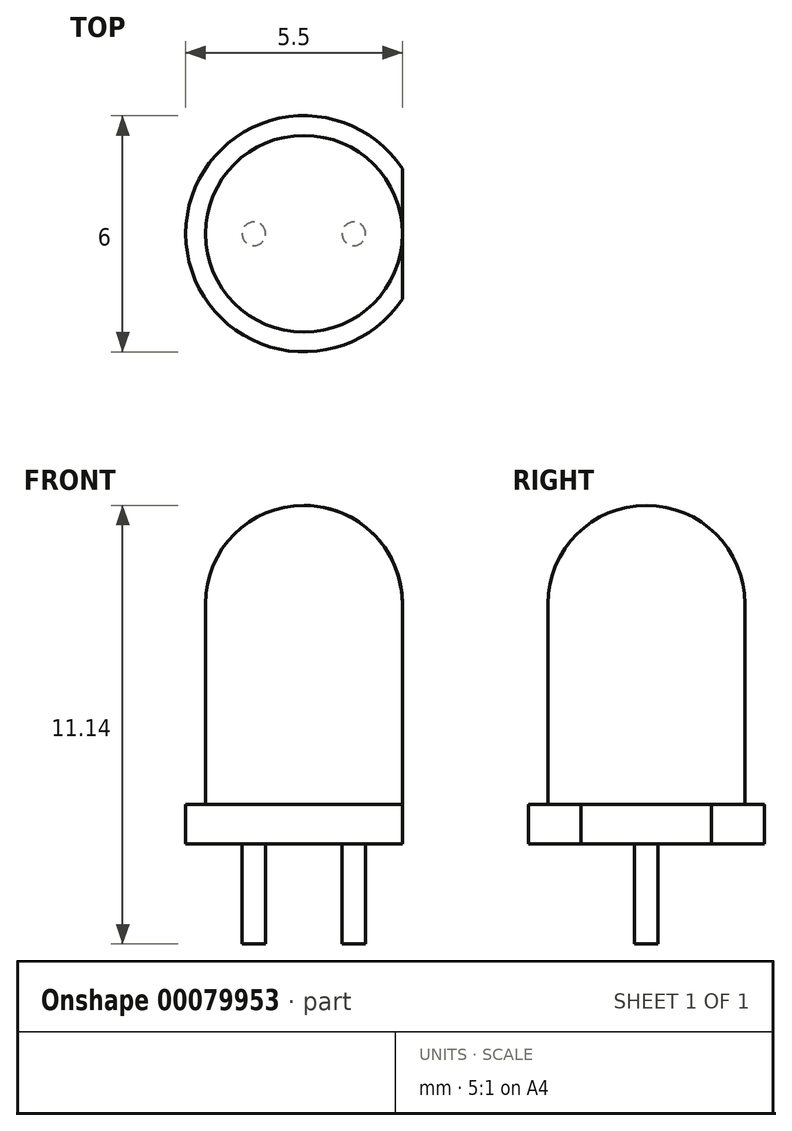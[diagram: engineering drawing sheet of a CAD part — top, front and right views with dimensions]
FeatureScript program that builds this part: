
annotation { "Feature Type Name" : "Feature", "Feature Type Description" : "" }
export const myFeature = defineFeature(function(context is Context, id is Id, definition is map)
    precondition{}
    {
        {
            var Q0;
            Q0=qCreatedBy(makeId("Top.planeOp"),FACE);
            var sketch = newSketch(context, id + "F0", { "sketchPlane" : qUnion([Q0])});
            skCircle(sketch, "E0", {"center": v(0, 0) * mm, "radius": 2.5 * mm});
            skCircle(sketch, "E1", {"center": v(0, 0) * mm, "radius": 3 * mm});
            skLineSegment(sketch, "E2", {"start": v(-1.27, 0) * mm, "end": v(1.27, 0) * mm});
            skCircle(sketch, "E3", {"center": v(-1.27, 0) * mm, "radius": 0.3 * mm});
            skCircle(sketch, "E4", {"center": v(1.27, 0) * mm, "radius": 0.3 * mm});
            skLineSegment(sketch, "E5", {"start": v(2.5, -1.66) * mm, "end": v(2.5, 1.66) * mm});
            skLineSegment(sketch, "E6", {"start": v(-2.69, -1.34) * mm, "end": v(0.18, -3) * mm});
            skLineSegment(sketch, "E7", {"start": v(-2.69, 1.34) * mm, "end": v(0.18, 3) * mm});
            skCircle(sketch, "E8", {"center": v(-0.64, -1.1) * mm, "radius": 0.3 * mm});
            skCircle(sketch, "E9", {"center": v(0.64, -1.1) * mm, "radius": 0.3 * mm});
            skCircle(sketch, "E10", {"center": v(0.64, 1.1) * mm, "radius": 0.3 * mm});
            skCircle(sketch, "E11", {"center": v(-0.64, 1.1) * mm, "radius": 0.3 * mm});
            skLineSegment(sketch, "E12", {"start": v(-0.64, -1.1) * mm, "end": v(-1.27, 0) * mm});
            skLineSegment(sketch, "E13", {"start": v(-0.64, -1.1) * mm, "end": v(0.64, -1.1) * mm});
            skLineSegment(sketch, "E14", {"start": v(0.63, -1.1) * mm, "end": v(1.27, 0) * mm});
            skLineSegment(sketch, "E15", {"start": v(1.27, 0) * mm, "end": v(0.63, 1.1) * mm});
            skLineSegment(sketch, "E16", {"start": v(-0.64, 1.1) * mm, "end": v(0.64, 1.1) * mm});
            skLineSegment(sketch, "E17", {"start": v(-0.64, 1.1) * mm, "end": v(-1.27, 0) * mm});
            skLineSegment(sketch, "E18", {"start": v(-0.64, -1.1) * mm, "end": v(0.64, 1.1) * mm});
            skLineSegment(sketch, "E19", {"start": v(-0.63, 1.1) * mm, "end": v(0.63, -1.1) * mm});
            skSolve(sketch);
        }
        {
            var Q0;
            Q0=makeQuery(id+"F0.imprint","IMPRINT",FACE,{"disambiguationData":[TD([[makeQuery(id+"F0.imprint","IMPRINT",EDGE,{"derivedFrom":sQuery(id+"F0.wireOp",EDGE,"E0")}),1.0]])]});
            var Q1;
            Q1=makeQuery(id+"F0.imprint","IMPRINT",FACE,{"disambiguationData":[TD([[makeQuery(id+"F0.imprint","IMPRINT",EDGE,{"derivedFrom":sQuery(id+"F0.wireOp",EDGE,"E3")}),1.0]])]});
            var Q2;
            Q2=makeQuery(id+"F0.imprint","IMPRINT",FACE,{"disambiguationData":[TD([[makeQuery(id+"F0.imprint","IMPRINT",EDGE,{"derivedFrom":sQuery(id+"F0.wireOp",EDGE,"E4")}),1.0]])]});
            var Q3;
            {var subQ1=sQuery(id+"F0.wireOp",EDGE,"E3");var subQ7=sQuery(id+"F0.wireOp",EDGE,"E2");var subQ8=makeQuery(id+"F0.imprint","INTERSECT",VERTEX,{"derivedFrom":[subQ7,subQ1]});Q3=makeQuery(id+"F0.imprint","IMPRINT",FACE,{"disambiguationData":[TD([[makeQuery(id+"F0.imprint","IMPRINT",EDGE,{"disambiguationData":[TD([[subQ8,1.0]])],"derivedFrom":subQ1}),-1.0]])]});}
            var Q4;
            {var subQ0=sQuery(id+"F0.wireOp",EDGE,"E18");var subQ1=sQuery(id+"F0.wireOp",EDGE,"E8");var subQ2=makeQuery(id+"F0.imprint","INTERSECT",VERTEX,{"derivedFrom":[subQ1,subQ0]});Q4=makeQuery(id+"F0.imprint","IMPRINT",FACE,{"disambiguationData":[TD([[makeQuery(id+"F0.imprint","IMPRINT",EDGE,{"disambiguationData":[TD([[subQ2,1.0]])],"derivedFrom":subQ1}),1.0]])]});}
            var Q5;
            {var subQ0=sQuery(id+"F0.wireOp",EDGE,"E18");var subQ1=sQuery(id+"F0.wireOp",EDGE,"E8");var subQ2=makeQuery(id+"F0.imprint","INTERSECT",VERTEX,{"derivedFrom":[subQ1,subQ0]});Q5=makeQuery(id+"F0.imprint","IMPRINT",FACE,{"disambiguationData":[TD([[makeQuery(id+"F0.imprint","IMPRINT",EDGE,{"disambiguationData":[TD([[subQ2,-1.0]])],"derivedFrom":subQ1}),1.0]])]});}
            var Q6;
            {var subQ0=sQuery(id+"F0.wireOp",EDGE,"E13");var subQ1=sQuery(id+"F0.wireOp",EDGE,"E8");var subQ2=makeQuery(id+"F0.imprint","INTERSECT",VERTEX,{"derivedFrom":[subQ1,subQ0]});Q6=makeQuery(id+"F0.imprint","IMPRINT",FACE,{"disambiguationData":[TD([[makeQuery(id+"F0.imprint","IMPRINT",EDGE,{"disambiguationData":[TD([[subQ2,1.0]])],"derivedFrom":subQ1}),1.0]])]});}
            var Q7;
            {var subQ5=sQuery(id+"F0.wireOp",EDGE,"E18");var subQ6=sQuery(id+"F0.wireOp",EDGE,"E8");var subQ7=makeQuery(id+"F0.imprint","INTERSECT",VERTEX,{"derivedFrom":[subQ6,subQ5]});Q7=makeQuery(id+"F0.imprint","IMPRINT",FACE,{"disambiguationData":[TD([[makeQuery(id+"F0.imprint","IMPRINT",EDGE,{"disambiguationData":[TD([[subQ7,1.0]])],"derivedFrom":subQ6}),-1.0]])]});}
            var Q8;
            {var subQ1=sQuery(id+"F0.wireOp",EDGE,"E3");var subQ7=sQuery(id+"F0.wireOp",EDGE,"E2");var subQ9=makeQuery(id+"F0.imprint","INTERSECT",VERTEX,{"derivedFrom":[subQ7,subQ1]});Q8=makeQuery(id+"F0.imprint","IMPRINT",FACE,{"disambiguationData":[TD([[makeQuery(id+"F0.imprint","IMPRINT",EDGE,{"disambiguationData":[TD([[subQ9,-1.0]])],"derivedFrom":subQ1}),-1.0]])]});}
            var Q9;
            {var subQ0=sQuery(id+"F0.wireOp",EDGE,"E17");var subQ1=sQuery(id+"F0.wireOp",EDGE,"E11");var subQ2=makeQuery(id+"F0.imprint","INTERSECT",VERTEX,{"derivedFrom":[subQ1,subQ0]});Q9=makeQuery(id+"F0.imprint","IMPRINT",FACE,{"disambiguationData":[TD([[makeQuery(id+"F0.imprint","IMPRINT",EDGE,{"disambiguationData":[TD([[subQ2,-1.0]])],"derivedFrom":subQ1}),1.0]])]});}
            var Q10;
            {var subQ0=sQuery(id+"F0.wireOp",EDGE,"E16");var subQ1=sQuery(id+"F0.wireOp",EDGE,"E11");var subQ2=makeQuery(id+"F0.imprint","INTERSECT",VERTEX,{"derivedFrom":[subQ1,subQ0]});Q10=makeQuery(id+"F0.imprint","IMPRINT",FACE,{"disambiguationData":[TD([[makeQuery(id+"F0.imprint","IMPRINT",EDGE,{"disambiguationData":[TD([[subQ2,1.0]])],"derivedFrom":subQ1}),1.0]])]});}
            var Q11;
            {var subQ0=sQuery(id+"F0.wireOp",EDGE,"E17");var subQ1=sQuery(id+"F0.wireOp",EDGE,"E11");var subQ2=makeQuery(id+"F0.imprint","INTERSECT",VERTEX,{"derivedFrom":[subQ1,subQ0]});Q11=makeQuery(id+"F0.imprint","IMPRINT",FACE,{"disambiguationData":[TD([[makeQuery(id+"F0.imprint","IMPRINT",EDGE,{"disambiguationData":[TD([[subQ2,1.0]])],"derivedFrom":subQ1}),1.0]])]});}
            var Q12;
            {var subQ0=sQuery(id+"F0.wireOp",EDGE,"E18");var subQ1=sQuery(id+"F0.wireOp",EDGE,"E10");var subQ2=makeQuery(id+"F0.imprint","INTERSECT",VERTEX,{"derivedFrom":[subQ1,subQ0]});Q12=makeQuery(id+"F0.imprint","IMPRINT",FACE,{"disambiguationData":[TD([[makeQuery(id+"F0.imprint","IMPRINT",EDGE,{"disambiguationData":[TD([[subQ2,1.0]])],"derivedFrom":subQ1}),-1.0]])]});}
            var Q13;
            {var subQ1=sQuery(id+"F0.wireOp",EDGE,"E4");var subQ7=sQuery(id+"F0.wireOp",EDGE,"E2");var subQ8=makeQuery(id+"F0.imprint","INTERSECT",VERTEX,{"derivedFrom":[subQ7,subQ1]});Q13=makeQuery(id+"F0.imprint","IMPRINT",FACE,{"disambiguationData":[TD([[makeQuery(id+"F0.imprint","IMPRINT",EDGE,{"disambiguationData":[TD([[subQ8,1.0]])],"derivedFrom":subQ1}),-1.0]])]});}
            var Q14;
            {var subQ1=sQuery(id+"F0.wireOp",EDGE,"E4");var subQ7=sQuery(id+"F0.wireOp",EDGE,"E2");var subQ9=makeQuery(id+"F0.imprint","INTERSECT",VERTEX,{"derivedFrom":[subQ7,subQ1]});Q14=makeQuery(id+"F0.imprint","IMPRINT",FACE,{"disambiguationData":[TD([[makeQuery(id+"F0.imprint","IMPRINT",EDGE,{"disambiguationData":[TD([[subQ9,-1.0]])],"derivedFrom":subQ1}),-1.0]])]});}
            var Q15;
            {var subQ0=sQuery(id+"F0.wireOp",EDGE,"E19");var subQ1=sQuery(id+"F0.wireOp",EDGE,"E9");var subQ2=makeQuery(id+"F0.imprint","INTERSECT",VERTEX,{"derivedFrom":[subQ1,subQ0]});Q15=makeQuery(id+"F0.imprint","IMPRINT",FACE,{"disambiguationData":[TD([[makeQuery(id+"F0.imprint","IMPRINT",EDGE,{"disambiguationData":[TD([[subQ2,1.0]])],"derivedFrom":subQ1}),1.0]])]});}
            var Q16;
            {var subQ0=sQuery(id+"F0.wireOp",EDGE,"E19");var subQ1=sQuery(id+"F0.wireOp",EDGE,"E9");var subQ2=makeQuery(id+"F0.imprint","INTERSECT",VERTEX,{"derivedFrom":[subQ1,subQ0]});Q16=makeQuery(id+"F0.imprint","IMPRINT",FACE,{"disambiguationData":[TD([[makeQuery(id+"F0.imprint","IMPRINT",EDGE,{"disambiguationData":[TD([[subQ2,-1.0]])],"derivedFrom":subQ1}),1.0]])]});}
            var Q17;
            {var subQ0=sQuery(id+"F0.wireOp",EDGE,"E14");var subQ1=sQuery(id+"F0.wireOp",EDGE,"E9");var subQ2=makeQuery(id+"F0.imprint","INTERSECT",VERTEX,{"derivedFrom":[subQ1,subQ0]});Q17=makeQuery(id+"F0.imprint","IMPRINT",FACE,{"disambiguationData":[TD([[makeQuery(id+"F0.imprint","IMPRINT",EDGE,{"disambiguationData":[TD([[subQ2,1.0]])],"derivedFrom":subQ1}),1.0]])]});}
            var Q18;
            {var subQ0=sQuery(id+"F0.wireOp",EDGE,"E18");var subQ1=sQuery(id+"F0.wireOp",EDGE,"E10");var subQ2=makeQuery(id+"F0.imprint","INTERSECT",VERTEX,{"derivedFrom":[subQ1,subQ0]});Q18=makeQuery(id+"F0.imprint","IMPRINT",FACE,{"disambiguationData":[TD([[makeQuery(id+"F0.imprint","IMPRINT",EDGE,{"disambiguationData":[TD([[subQ2,-1.0]])],"derivedFrom":subQ1}),1.0]])]});}
            var Q19;
            {var subQ0=sQuery(id+"F0.wireOp",EDGE,"E18");var subQ1=sQuery(id+"F0.wireOp",EDGE,"E10");var subQ2=makeQuery(id+"F0.imprint","INTERSECT",VERTEX,{"derivedFrom":[subQ1,subQ0]});Q19=makeQuery(id+"F0.imprint","IMPRINT",FACE,{"disambiguationData":[TD([[makeQuery(id+"F0.imprint","IMPRINT",EDGE,{"disambiguationData":[TD([[subQ2,1.0]])],"derivedFrom":subQ1}),1.0]])]});}
            var Q20;
            {var subQ0=sQuery(id+"F0.wireOp",EDGE,"E16");var subQ1=sQuery(id+"F0.wireOp",EDGE,"E10");var subQ2=makeQuery(id+"F0.imprint","INTERSECT",VERTEX,{"derivedFrom":[subQ1,subQ0]});Q20=makeQuery(id+"F0.imprint","IMPRINT",FACE,{"disambiguationData":[TD([[makeQuery(id+"F0.imprint","IMPRINT",EDGE,{"disambiguationData":[TD([[subQ2,1.0]])],"derivedFrom":subQ1}),1.0]])]});}
            extrude(context, id + "F1", {"entities" : qUnion([Q0, Q1, Q2, Q3, Q4, Q5, Q6, Q7, Q8, Q9, Q10, Q11, Q12, Q13, Q14, Q15, Q16, Q17, Q18, Q19, Q20]), "depth" : 8.6 * mm});
        }
        {
            var Q0;
            Q0=makeQuery(id+"F1.opExtrude","CAP_EDGE",EDGE,{"disambiguationData":[OSD([sQuery(id+"F0.wireOp",EDGE,"E0")])],"isStart":false});
            fillet(context, id + "F2", {"entities" : qUnion([Q0]), "radius" : 5 * mm / 2, "tangentPropagation" : true, "allowEdgeOverflow" : false});
        }
        {
            var Q0;
            {var subQ0=sQuery(id+"F0.wireOp",EDGE,"E0");Q0=makeQuery(id+"F0.imprint","IMPRINT",FACE,{"disambiguationData":[TD([[makeQuery(id+"F0.imprint","IMPRINT",EDGE,{"derivedFrom":subQ0}),-1.0]])]});}
            var Q1;
            {var subQ0=sQuery(id+"F0.wireOp",EDGE,"E6");Q1=makeQuery(id+"F0.imprint","IMPRINT",FACE,{"disambiguationData":[TD([[makeQuery(id+"F0.imprint","IMPRINT",EDGE,{"derivedFrom":subQ0}),-1.0]])]});}
            var Q2;
            {var subQ0=sQuery(id+"F0.wireOp",EDGE,"E7");Q2=makeQuery(id+"F0.imprint","IMPRINT",FACE,{"disambiguationData":[TD([[makeQuery(id+"F0.imprint","IMPRINT",EDGE,{"derivedFrom":subQ0}),1.0]])]});}
            extrude(context, id + "F3", {"entities" : qUnion([Q0, Q1, Q2]), "operationType" : NewBodyOperationType.ADD, "depth" : 1 * mm});
        }
        {
            var Q0;
            Q0=makeQuery(id+"F0.imprint","IMPRINT",FACE,{"disambiguationData":[TD([[makeQuery(id+"F0.imprint","IMPRINT",EDGE,{"derivedFrom":sQuery(id+"F0.wireOp",EDGE,"E4")}),1.0]])]});
            extrude(context, id + "F4", {"entities" : qUnion([Q0]), "operationType" : NewBodyOperationType.ADD, "oppositeDirection" : true, "depth" : 2.54 * mm});
        }
        {
            var Q0;
            Q0=makeQuery(id+"F0.imprint","IMPRINT",FACE,{"disambiguationData":[TD([[makeQuery(id+"F0.imprint","IMPRINT",EDGE,{"derivedFrom":sQuery(id+"F0.wireOp",EDGE,"E3")}),1.0]])]});
            extrude(context, id + "F5", {"entities" : qUnion([Q0]), "operationType" : NewBodyOperationType.ADD, "oppositeDirection" : true, "depth" : 2.54 * mm});
        }
    });
